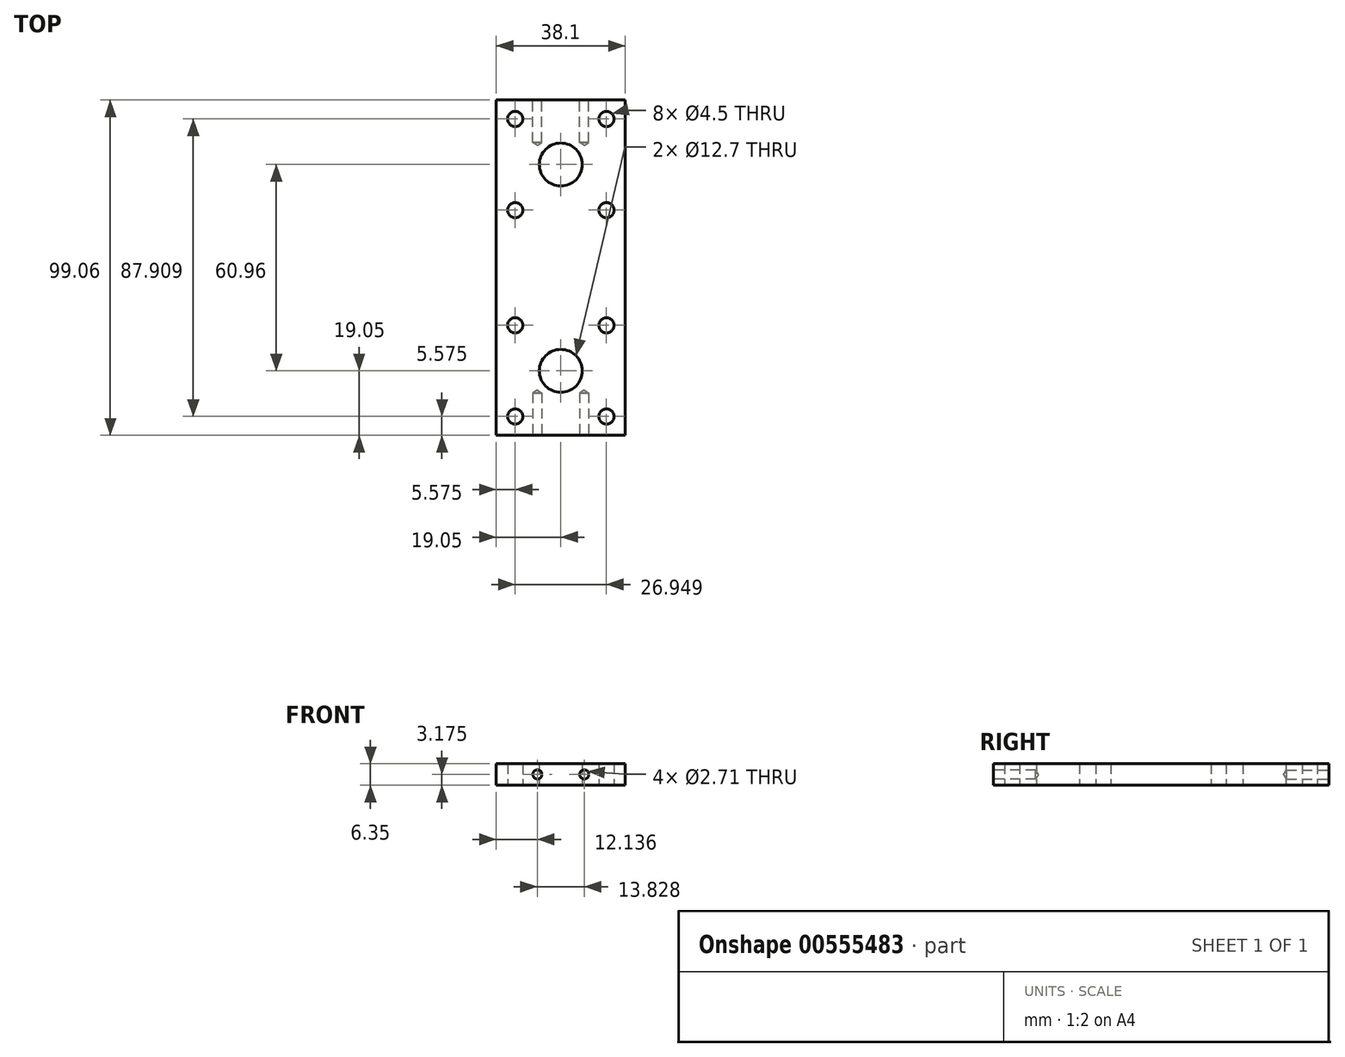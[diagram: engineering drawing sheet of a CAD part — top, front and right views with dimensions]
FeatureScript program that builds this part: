
annotation { "Feature Type Name" : "Feature", "Feature Type Description" : "" }
export const myFeature = defineFeature(function(context is Context, id is Id, definition is map)
    precondition{}
    {
        {
            var Q0;
            Q0=qCreatedBy(makeId("Top.planeOp"),FACE);
            var sketch = newSketch(context, id + "F0", { "sketchPlane" : qUnion([Q0])});
            skLineSegment(sketch, "E0.bottom", {"start": v(-19.05, 19.05) * mm, "end": v(19.05, 19.05) * mm});
            skLineSegment(sketch, "E0.top", {"start": v(-19.05, -19.05) * mm, "end": v(19.05, -19.05) * mm});
            skLineSegment(sketch, "E0.left", {"start": v(-19.05, 19.05) * mm, "end": v(-19.05, -19.05) * mm});
            skLineSegment(sketch, "E0.right", {"start": v(19.05, 19.05) * mm, "end": v(19.05, -19.05) * mm});
            skPoint(sketch, "E0.middle", {"position": v(0, 0) * mm});
            skLineSegment(sketch, "E1", {"start": v(-19.05, 13.47) * mm, "end": v(19.05, 13.47) * mm, "construction": true});
            skLineSegment(sketch, "E2", {"start": v(-13.47, 19.05) * mm, "end": v(-13.47, -19.05) * mm, "construction": true});
            skLineSegment(sketch, "E3", {"start": v(13.47, 19.05) * mm, "end": v(13.47, -19.05) * mm, "construction": true});
            skLineSegment(sketch, "E4", {"start": v(-19.05, -13.47) * mm, "end": v(19.05, -13.47) * mm, "construction": true});
            skLineSegment(sketch, "E5", {"start": v(-19.05, 0) * mm, "end": v(19.05, 0) * mm, "construction": true});
            skCircle(sketch, "E6", {"center": v(0, 0) * mm, "radius": 6.35 * mm});
            skPoint(sketch, "E7", {"position": v(-13.47, -13.47) * mm});
            skPoint(sketch, "E8", {"position": v(-13.47, 13.47) * mm});
            skPoint(sketch, "E9", {"position": v(13.47, 13.47) * mm});
            skPoint(sketch, "E10", {"position": v(13.47, -13.47) * mm});
            skLineSegment(sketch, "E11.bottom", {"start": v(-19.05, -41.91) * mm, "end": v(19.05, -41.91) * mm});
            skLineSegment(sketch, "E11.top", {"start": v(-19.05, -80) * mm, "end": v(19.05, -80) * mm});
            skLineSegment(sketch, "E11.left", {"start": v(-19.05, -41.91) * mm, "end": v(-19.05, -80) * mm});
            skLineSegment(sketch, "E11.right", {"start": v(19.05, -41.91) * mm, "end": v(19.05, -80) * mm});
            skPoint(sketch, "E11.middle", {"position": v(0, -60.96) * mm});
            skLineSegment(sketch, "E12", {"start": v(-19.05, -47.49) * mm, "end": v(19.05, -47.49) * mm, "construction": true});
            skLineSegment(sketch, "E13", {"start": v(-13.47, -41.9) * mm, "end": v(-13.47, -80) * mm, "construction": true});
            skLineSegment(sketch, "E14", {"start": v(13.47, -41.9) * mm, "end": v(13.47, -80) * mm, "construction": true});
            skLineSegment(sketch, "E15", {"start": v(-19.05, -74.43) * mm, "end": v(19.05, -74.43) * mm, "construction": true});
            skLineSegment(sketch, "E16", {"start": v(-19.05, -60.96) * mm, "end": v(19.05, -60.96) * mm, "construction": true});
            skCircle(sketch, "E17", {"center": v(0, -60.96) * mm, "radius": 6.35 * mm});
            skPoint(sketch, "E18", {"position": v(-13.47, -74.43) * mm});
            skPoint(sketch, "E19", {"position": v(-13.47, -47.49) * mm});
            skPoint(sketch, "E20", {"position": v(13.47, -47.49) * mm});
            skPoint(sketch, "E21", {"position": v(13.47, -74.43) * mm});
            skLineSegment(sketch, "E22", {"start": v(-19.05, -19.05) * mm, "end": v(-19.05, -41.91) * mm});
            skLineSegment(sketch, "E23", {"start": v(19.05, -19.05) * mm, "end": v(19.05, -41.91) * mm});
            skSolve(sketch);
        }
        {
            var Q0;
            {var subQ0=sQuery(id+"F0.wireOp",EDGE,"E0.right");Q0=makeQuery(id+"F0.imprint","IMPRINT",FACE,{"disambiguationData":[TD([[makeQuery(id+"F0.imprint","IMPRINT",EDGE,{"derivedFrom":subQ0}),-1.0]])]});}
            var Q1;
            Q1=makeQuery(id+"F0.imprint","IMPRINT",FACE,{"disambiguationData":[TD([[makeQuery(id+"F0.imprint","IMPRINT",EDGE,{"derivedFrom":sQuery(id+"F0.wireOp",EDGE,"E0.top")}),-1.0]])]});
            var Q2;
            Q2=makeQuery(id+"F0.imprint","IMPRINT",FACE,{"disambiguationData":[TD([[makeQuery(id+"F0.imprint","IMPRINT",EDGE,{"derivedFrom":sQuery(id+"F0.wireOp",EDGE,"E11.bottom")}),-1.0]])]});
            extrude(context, id + "F1", {"entities" : qUnion([Q0, Q1, Q2]), "depth" : 6.35 * mm, "offsetDistance" : 25.4 * mm});
        }
        {
            var Q0;
            Q0=sQuery(id+"F0.wireOp",VERTEX,"E8");
            var Q1;
            Q1=sQuery(id+"F0.wireOp",VERTEX,"E9");
            var Q2;
            Q2=sQuery(id+"F0.wireOp",VERTEX,"E10");
            var Q3;
            Q3=sQuery(id+"F0.wireOp",VERTEX,"E7");
            var Q4;
            Q4=sQuery(id+"F0.wireOp",VERTEX,"E19");
            var Q5;
            Q5=sQuery(id+"F0.wireOp",VERTEX,"E20");
            var Q6;
            Q6=sQuery(id+"F0.wireOp",VERTEX,"E21");
            var Q7;
            Q7=sQuery(id+"F0.wireOp",VERTEX,"E18");
            var Q8;
            Q8=makeQuery(id+"F1.opExtrude","SWEPT_BODY",BODY,{"disambiguationData":[OSD([sQuery(id+"F0.wireOp",EDGE,"E0.bottom"),sQuery(id+"F0.wireOp",EDGE,"E0.left"),sQuery(id+"F0.wireOp",EDGE,"E0.right"),sQuery(id+"F0.wireOp",EDGE,"E6"),sQuery(id+"F0.wireOp",EDGE,"E11.top"),sQuery(id+"F0.wireOp",EDGE,"E11.left"),sQuery(id+"F0.wireOp",EDGE,"E11.right"),sQuery(id+"F0.wireOp",EDGE,"E17"),sQuery(id+"F0.wireOp",EDGE,"E22"),sQuery(id+"F0.wireOp",EDGE,"E23")])]});
            hole(context, id + "F2", {"style" : HoleStyle.SIMPLE, "endStyle" : HoleEndStyle.THROUGH, "oppositeDirection" : true, "standardTappedOrClearance" : lookupTablePath({ "standard" : "ANSI", "fit" : "Normal (ASME)", "size" : "#8", "type" : "Clearance" }), "standardBlindInLast" : lookupTablePath({ "fit" : "Free", "standard" : "ANSI", "size" : "#8", "type" : "Clearance" }), "holeDiameter" : 4.5 * mm, "isTappedThrough" : true, "tappedDepth" : 12.7 * mm, "tapClearance" : 3, "locations" : qUnion([Q0, Q1, Q2, Q3, Q4, Q5, Q6, Q7]), "scope" : qUnion([Q8])});
        }
        {
            var Q0;
            Q0=makeQuery(id+"F1.opExtrude","SWEPT_FACE",FACE,{"disambiguationData":[OSD([sQuery(id+"F0.wireOp",EDGE,"E11.top")])]});
            var sketch = newSketch(context, id + "F3", { "sketchPlane" : qUnion([Q0])});
            skLineSegment(sketch, "E24", {"start": v(-19.05, 3.18) * mm, "end": v(19.05, 3.18) * mm, "construction": true});
            skPoint(sketch, "E25", {"position": v(-6.91, 3.17) * mm});
            skPoint(sketch, "E26", {"position": v(6.91, 3.18) * mm});
            skPoint(sketch, "E27", {"position": v(0, 3.18) * mm});
            skSolve(sketch);
        }
        {
            var Q0;
            Q0=makeQuery(id+"F1.opExtrude","SWEPT_FACE",FACE,{"disambiguationData":[OSD([sQuery(id+"F0.wireOp",EDGE,"E0.bottom")])]});
            var sketch = newSketch(context, id + "F4", { "sketchPlane" : qUnion([Q0])});
            skLineSegment(sketch, "E28", {"start": v(-19.05, 3.18) * mm, "end": v(19.05, 3.18) * mm, "construction": true});
            skPoint(sketch, "E29", {"position": v(-6.91, 3.17) * mm});
            skPoint(sketch, "E30", {"position": v(6.91, 3.18) * mm});
            skPoint(sketch, "E31", {"position": v(0, 3.18) * mm});
            skSolve(sketch);
        }
        {
            var Q0;
            Q0=sQuery(id+"F4.wireOp",VERTEX,"E29");
            var Q1;
            Q1=sQuery(id+"F4.wireOp",VERTEX,"E30");
            var Q2;
            Q2=sQuery(id+"F3.wireOp",VERTEX,"E26");
            var Q3;
            Q3=sQuery(id+"F3.wireOp",VERTEX,"E25");
            var Q4;
            Q4=makeQuery(id+"F1.opExtrude","SWEPT_BODY",BODY,{"disambiguationData":[OSD([sQuery(id+"F0.wireOp",EDGE,"E0.bottom"),sQuery(id+"F0.wireOp",EDGE,"E0.left"),sQuery(id+"F0.wireOp",EDGE,"E0.right"),sQuery(id+"F0.wireOp",EDGE,"E6"),sQuery(id+"F0.wireOp",EDGE,"E11.top"),sQuery(id+"F0.wireOp",EDGE,"E11.left"),sQuery(id+"F0.wireOp",EDGE,"E11.right"),sQuery(id+"F0.wireOp",EDGE,"E17"),sQuery(id+"F0.wireOp",EDGE,"E22"),sQuery(id+"F0.wireOp",EDGE,"E23")])]});
            hole(context, id + "F5", {"style" : HoleStyle.SIMPLE, "endStyle" : HoleEndStyle.BLIND, "standardTappedOrClearance" : lookupTablePath({ "standard" : "ANSI", "engagement" : "75%", "pitch" : "32 tpi", "size" : "#6", "type" : "Tapped" }), "standardBlindInLast" : lookupTablePath({ "standard" : "ANSI", "engagement" : "75%", "pitch" : "32 tpi", "size" : "#6", "type" : "Tapped" }), "holeDiameter" : 2.7 * mm, "showTappedDepth" : true, "holeDepth" : 12.54 * mm, "isTappedThrough" : true, "tappedDepth" : 10.16 * mm, "tapClearance" : 3, "locations" : qUnion([Q0, Q1, Q2, Q3]), "scope" : qUnion([Q4]), "majorDiameter" : 3.5 * mm});
        }
    });
